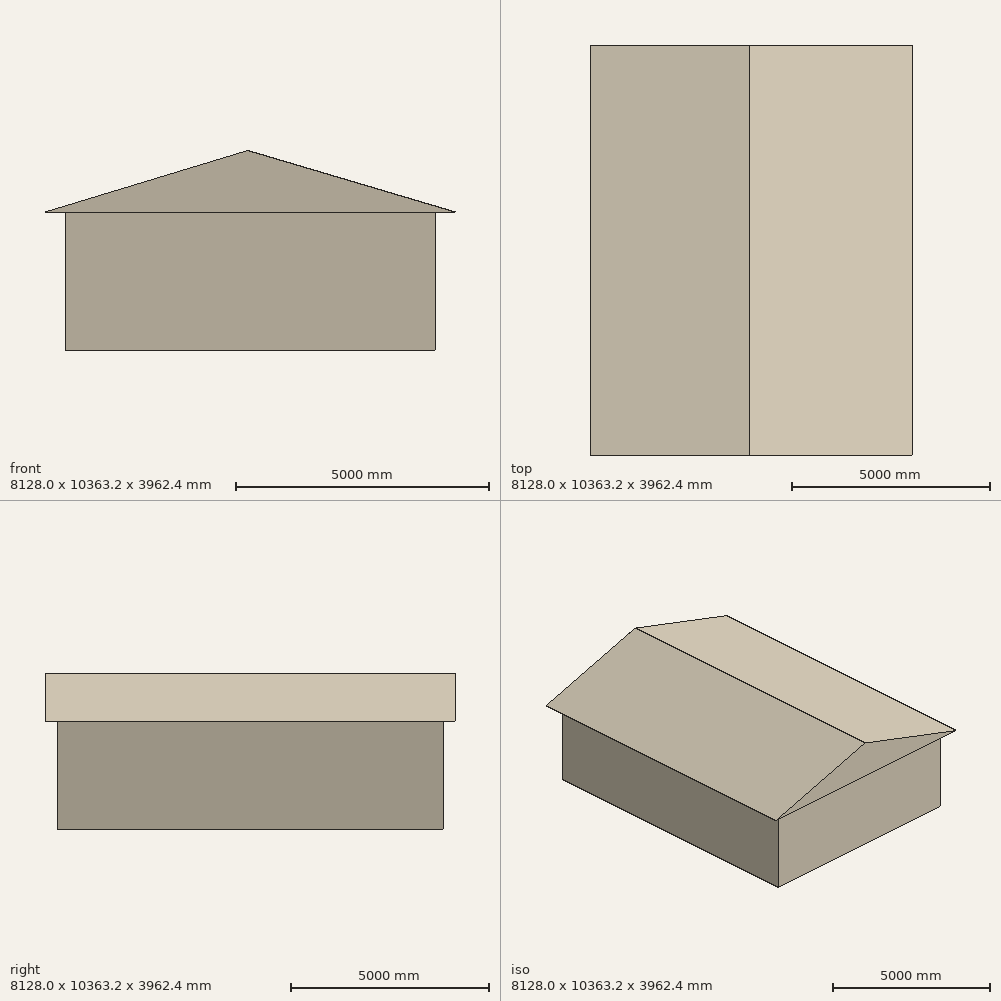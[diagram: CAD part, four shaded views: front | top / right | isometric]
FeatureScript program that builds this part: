
annotation { "Feature Type Name" : "Feature", "Feature Type Description" : "" }
export const myFeature = defineFeature(function(context is Context, id is Id, definition is map)
    precondition{}
    {
        {
            var Q0;
            Q0=qCreatedBy(makeId("Front.planeOp"),FACE);
            var sketch = newSketch(context, id + "F0", { "sketchPlane" : qUnion([Q0])});
            skLineSegment(sketch, "E0.bottom", {"start": v(-3609.16, 0) * mm, "end": v(3706.04, 0) * mm});
            skLineSegment(sketch, "E0.top", {"start": v(-3609.16, 2743.2) * mm, "end": v(3706.04, 2743.2) * mm});
            skLineSegment(sketch, "E0.left", {"start": v(-3609.16, 0) * mm, "end": v(-3609.16, 2743.2) * mm});
            skLineSegment(sketch, "E0.right", {"start": v(3706.04, 0) * mm, "end": v(3706.04, 2743.2) * mm});
            skSolve(sketch);
        }
        {
            var Q0;
            Q0 = qSketchRegion(id + "F0", true);
            extrude(context, id + "F1", {"entities" : qUnion([Q0]), "endBound" : BoundingType.SYMMETRIC, "depth" : 9753.6 * mm});
        }
        {
            var Q0;
            Q0=qCreatedBy(makeId("Front.planeOp"),FACE);
            var sketch = newSketch(context, id + "F2", { "sketchPlane" : qUnion([Q0])});
            skPoint(sketch, "E1.0", {"position": v(-3609.16, 2743.2) * mm});
            skPoint(sketch, "E2.0", {"position": v(3706.04, 2743.2) * mm});
            skLineSegment(sketch, "E3", {"start": v(-3609.16, 2743.2) * mm, "end": v(-4015.56, 2743.2) * mm});
            skLineSegment(sketch, "E4", {"start": v(-4015.56, 2743.2) * mm, "end": v(0, 3962.4) * mm});
            skLineSegment(sketch, "E5", {"start": v(0, 3962.4) * mm, "end": v(4112.44, 2743.2) * mm});
            skLineSegment(sketch, "E6", {"start": v(4112.44, 2743.2) * mm, "end": v(3706.04, 2743.2) * mm});
            skLineSegment(sketch, "E7", {"start": v(3706.04, 2743.2) * mm, "end": v(-3609.16, 2743.2) * mm});
            skSolve(sketch);
        }
        {
            var Q0;
            Q0 = qSketchRegion(id + "F2", true);
            extrude(context, id + "F3", {"entities" : qUnion([Q0]), "operationType" : NewBodyOperationType.ADD, "endBound" : BoundingType.SYMMETRIC, "depth" : 10363.2 * mm});
        }
    });
